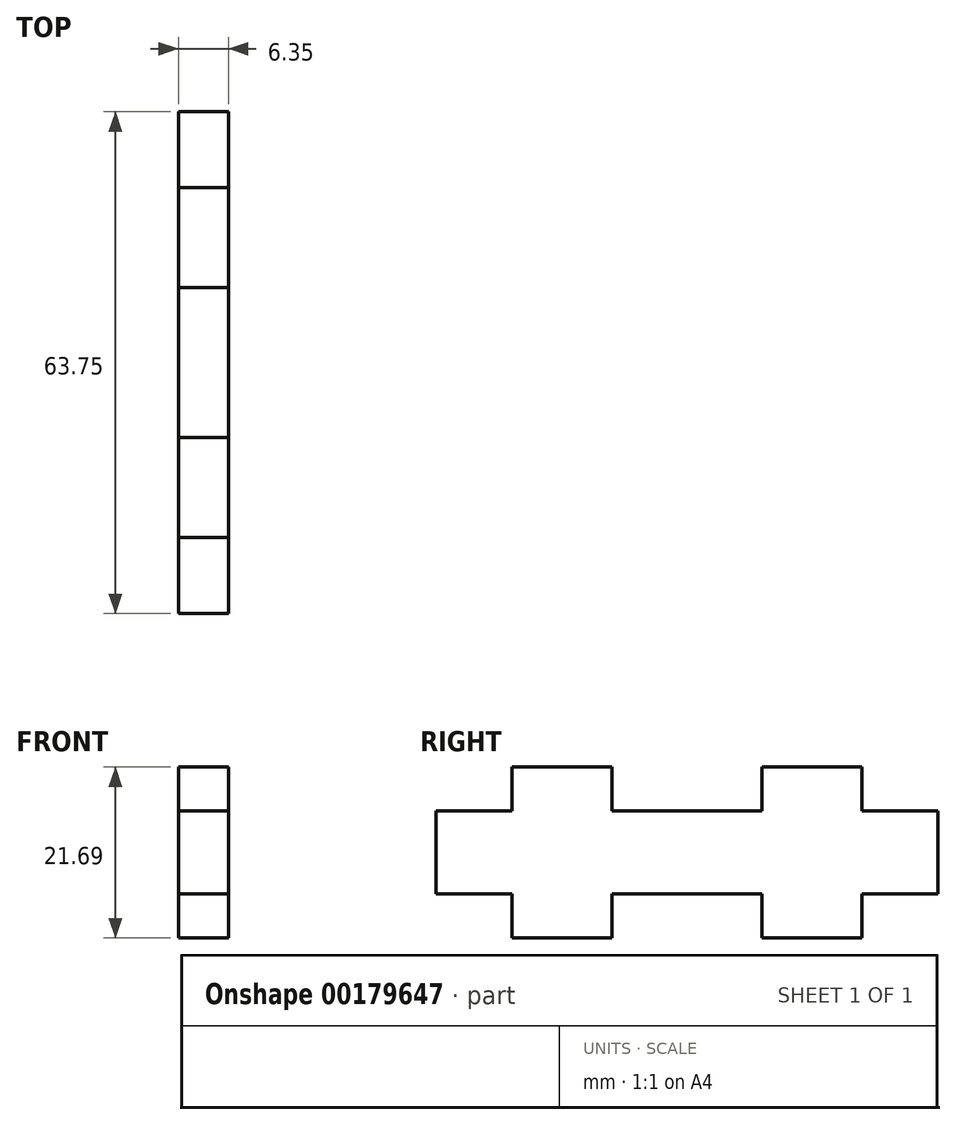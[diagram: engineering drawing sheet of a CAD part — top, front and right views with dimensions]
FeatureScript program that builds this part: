
annotation { "Feature Type Name" : "Feature", "Feature Type Description" : "" }
export const myFeature = defineFeature(function(context is Context, id is Id, definition is map)
    precondition{}
    {
        {
            var Q0;
            Q0=qCreatedBy(makeId("Right.planeOp"),FACE);
            var sketch = newSketch(context, id + "F0", { "sketchPlane" : qUnion([Q0])});
            skLineSegment(sketch, "E0", {"start": v(0.02, 67.96) * mm, "end": v(0.02, -68.48) * mm});
            skLineSegment(sketch, "E1.bottom", {"start": v(-29.32, 78.67) * mm, "end": v(-19.67, 78.67) * mm});
            skLineSegment(sketch, "E1.top", {"start": v(-29.32, 68.15) * mm, "end": v(-19.67, 68.15) * mm});
            skLineSegment(sketch, "E1.left", {"start": v(-29.32, 78.67) * mm, "end": v(-29.32, 68.15) * mm});
            skLineSegment(sketch, "E1.right", {"start": v(34.43, 78.67) * mm, "end": v(34.43, 68.15) * mm});
            skLineSegment(sketch, "E2", {"start": v(-29.32, 73.4) * mm, "end": v(34.43, 73.4) * mm, "construction": true});
            skLineSegment(sketch, "E3", {"start": v(-19.67, 68.15) * mm, "end": v(-19.67, 62.56) * mm});
            skLineSegment(sketch, "E4", {"start": v(-19.67, 62.56) * mm, "end": v(-6.97, 62.56) * mm});
            skLineSegment(sketch, "E5", {"start": v(-6.97, 62.56) * mm, "end": v(-6.97, 68.15) * mm});
            skLineSegment(sketch, "E6.1.0.0", {"start": v(12.08, 68.15) * mm, "end": v(12.08, 62.56) * mm});
            skLineSegment(sketch, "E6.1.0.1", {"start": v(12.08, 62.56) * mm, "end": v(24.78, 62.56) * mm});
            skLineSegment(sketch, "E6.1.0.2", {"start": v(24.78, 62.56) * mm, "end": v(24.78, 68.15) * mm});
            skLineSegment(sketch, "E7.trimOffspring", {"start": v(-6.97, 68.15) * mm, "end": v(12.08, 68.15) * mm});
            skLineSegment(sketch, "E8.trimOffspring", {"start": v(24.78, 68.15) * mm, "end": v(34.43, 68.15) * mm});
            skLineSegment(sketch, "E9.MirrorCS", {"start": v(-19.67, 78.67) * mm, "end": v(-19.67, 84.25) * mm});
            skLineSegment(sketch, "E10.MirrorCS", {"start": v(-6.97, 84.25) * mm, "end": v(-6.97, 78.67) * mm});
            skLineSegment(sketch, "E11.MirrorCS", {"start": v(12.08, 78.67) * mm, "end": v(12.08, 84.25) * mm});
            skLineSegment(sketch, "E12.MirrorCS", {"start": v(12.08, 84.25) * mm, "end": v(24.78, 84.25) * mm});
            skLineSegment(sketch, "E13.MirrorCS", {"start": v(24.78, 84.25) * mm, "end": v(24.78, 78.67) * mm});
            skLineSegment(sketch, "E14.MirrorCS", {"start": v(-19.67, 84.25) * mm, "end": v(-6.97, 84.25) * mm});
            skLineSegment(sketch, "E15.trimOffspring", {"start": v(-6.97, 78.67) * mm, "end": v(12.08, 78.67) * mm});
            skLineSegment(sketch, "E16.trimOffspring", {"start": v(24.78, 78.67) * mm, "end": v(34.43, 78.67) * mm});
            skSolve(sketch);
        }
        {
            var Q0;
            Q0=makeQuery(id+"F0.imprint","IMPRINT",FACE,{"disambiguationData":[TD([[makeQuery(id+"F0.imprint","IMPRINT",EDGE,{"derivedFrom":sQuery(id+"F0.wireOp",EDGE,"E1.bottom")}),-1.0]])]});
            extrude(context, id + "F1", {"entities" : qUnion([Q0]), "depth" : 6.35 * mm});
        }
    });
